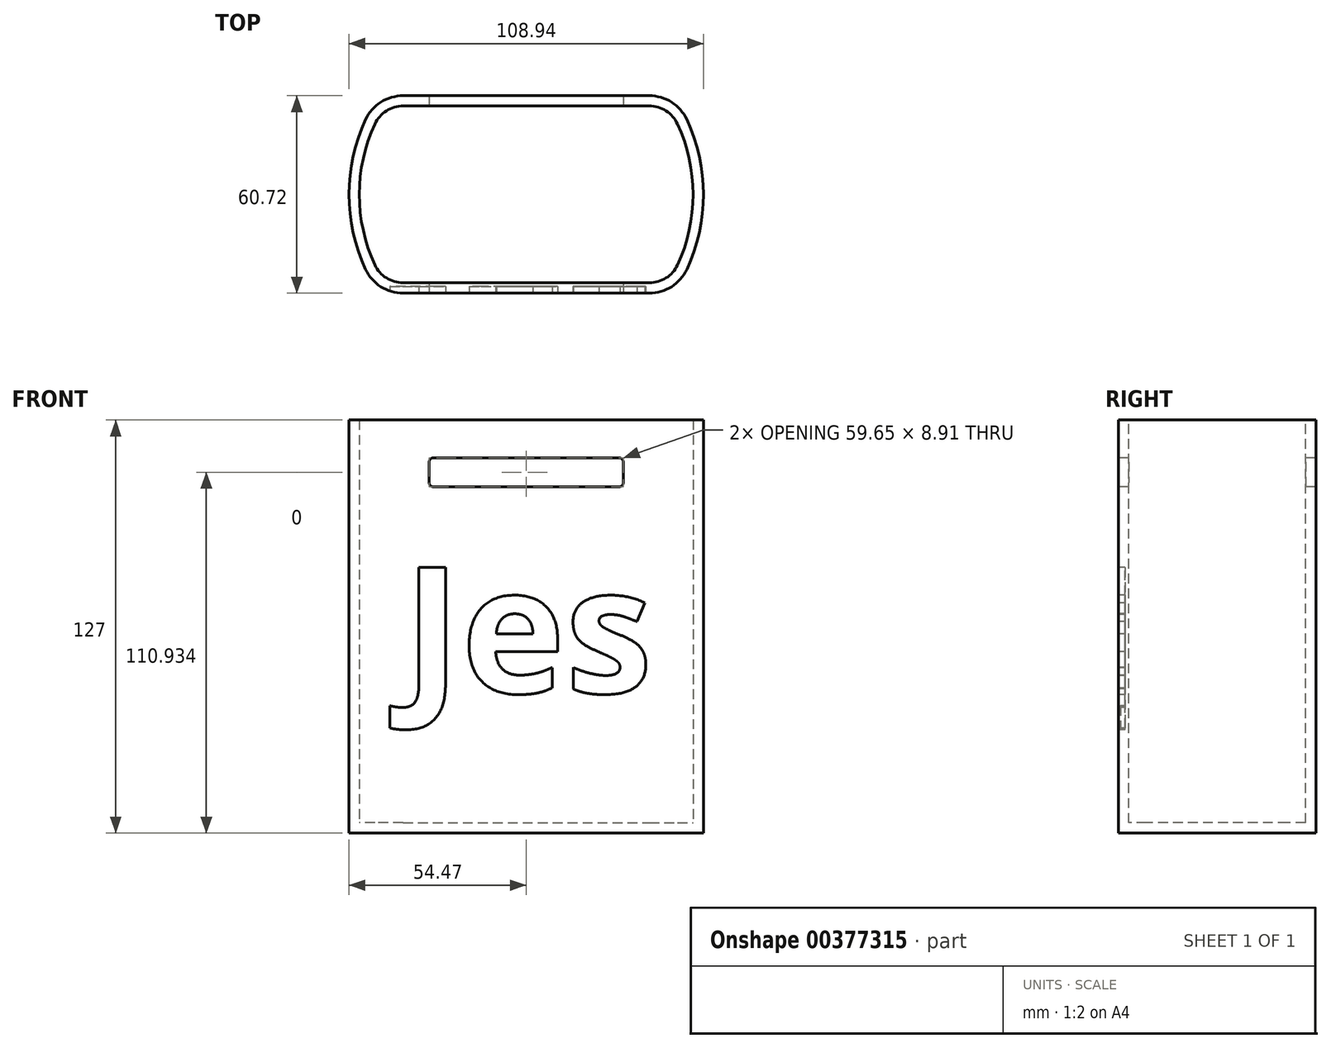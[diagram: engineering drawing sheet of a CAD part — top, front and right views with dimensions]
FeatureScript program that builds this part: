
annotation { "Feature Type Name" : "Feature", "Feature Type Description" : "" }
export const myFeature = defineFeature(function(context is Context, id is Id, definition is map)
    precondition{}
    {
        {
            var Q0;
            Q0=qCreatedBy(makeId("Top.planeOp"),FACE);
            var sketch = newSketch(context, id + "F0", { "sketchPlane" : qUnion([Q0])});
            skArc(sketch, "E0", {"start": v(-49.36, 23.02) * mm, "mid": v(-54.47, 0) * mm, "end": v(-49.36, -23.02) * mm});
            skLineSegment(sketch, "E1", {"start": v(-37.85, 30.36) * mm, "end": v(37.85, 30.36) * mm});
            skLineSegment(sketch, "E2", {"start": v(-54.47, 0) * mm, "end": v(54.47, 0) * mm, "construction": true});
            skLineSegment(sketch, "E3.MirrorCS", {"start": v(-37.85, -30.36) * mm, "end": v(37.85, -30.36) * mm});
            skArc(sketch, "E4.trimOffspring", {"start": v(49.36, -23.02) * mm, "mid": v(54.47, 0) * mm, "end": v(49.36, 23.02) * mm});
            skPoint(sketch, "E5.visualSharp", {"position": v(-45.22, 30.36) * mm});
            skArc(sketch, "E5.filletArc", {"start": v(-37.85, 30.36) * mm, "mid": v(-44.67, 28.37) * mm, "end": v(-49.36, 23.02) * mm});
            skPoint(sketch, "E6.visualSharp", {"position": v(45.22, 30.36) * mm});
            skArc(sketch, "E6.filletArc", {"start": v(49.36, 23.02) * mm, "mid": v(44.67, 28.37) * mm, "end": v(37.85, 30.36) * mm});
            skPoint(sketch, "E7.visualSharp", {"position": v(-45.22, -30.36) * mm});
            skArc(sketch, "E7.filletArc", {"start": v(-49.36, -23.02) * mm, "mid": v(-44.67, -28.37) * mm, "end": v(-37.85, -30.36) * mm});
            skPoint(sketch, "E8.visualSharp", {"position": v(45.22, -30.36) * mm});
            skArc(sketch, "E8.filletArc", {"start": v(37.85, -30.36) * mm, "mid": v(44.67, -28.37) * mm, "end": v(49.36, -23.02) * mm});
            skSolve(sketch);
        }
        {
            var Q0;
            Q0=makeQuery(id+"F0.imprint","IMPRINT",FACE,{"disambiguationData":[TD([[makeQuery(id+"F0.imprint","IMPRINT",EDGE,{"derivedFrom":sQuery(id+"F0.wireOp",EDGE,"E0")}),1.0]])]});
            extrude(context, id + "F1", {"entities" : qUnion([Q0]), "depth" : 127 * mm});
        }
        {
            var Q0;
            Q0=makeQuery(id+"F1.opExtrude","CAP_FACE",FACE,{"disambiguationData":[OSD([sQuery(id+"F0.wireOp",EDGE,"E0"),sQuery(id+"F0.wireOp",EDGE,"E1"),sQuery(id+"F0.wireOp",EDGE,"E3.MirrorCS"),sQuery(id+"F0.wireOp",EDGE,"E4.trimOffspring"),sQuery(id+"F0.wireOp",EDGE,"E5.filletArc"),sQuery(id+"F0.wireOp",EDGE,"E6.filletArc"),sQuery(id+"F0.wireOp",EDGE,"E7.filletArc"),sQuery(id+"F0.wireOp",EDGE,"E8.filletArc")])],"isStart":false});
            shell(context, id + "F2", {"entities" : qUnion([Q0]), "thickness" : 3.17 * mm});
        }
        {
            var Q0;
            Q0=makeQuery(id+"F1.opExtrude","SWEPT_FACE",FACE,{"disambiguationData":[OSD([sQuery(id+"F0.wireOp",EDGE,"E3.MirrorCS")])]});
            var sketch = newSketch(context, id + "F3", { "sketchPlane" : qUnion([Q0])});
            skText(sketch, "E9", { "text": "Jes", "fontName": "OpenSans-Bold.ttf"});
            const initialGuessF3  = {"E9": [-0.03785, 0.04312, 1, 0, 0.0389]};
            skSetInitialGuess(sketch, initialGuessF3);
            skSolve(sketch);
        }
        {
            var Q0;
            Q0 = qSketchRegion(id + "F3", true);
            extrude(context, id + "F4", {"entities" : qUnion([Q0]), "operationType" : NewBodyOperationType.REMOVE, "oppositeDirection" : true, "depth" : 2.03 * mm});
        }
        {
            var Q0;
            {var subQ1=sQuery(id+"F0.wireOp",EDGE,"E7.filletArc");var subQ5=sQuery(id+"F0.wireOp",EDGE,"E3.MirrorCS");Q0=makeQuery(id+"F4.boolean.opBoolean","SPLIT",FACE,{"disambiguationData":[TD([makeQuery(id+"F1.opExtrude","SWEPT_FACE",FACE,{"disambiguationData":[OSD([subQ1])]})])],"derivedFrom":makeQuery(id+"F1.opExtrude","SWEPT_FACE",FACE,{"disambiguationData":[OSD([subQ5])]})});}
            var sketch = newSketch(context, id + "F5", { "sketchPlane" : qUnion([Q0])});
            skLineSegment(sketch, "E10.bottom", {"start": v(28.55, 106.48) * mm, "end": v(-28.55, 106.48) * mm});
            skLineSegment(sketch, "E10.top", {"start": v(28.55, 115.39) * mm, "end": v(-28.55, 115.39) * mm});
            skLineSegment(sketch, "E10.left", {"start": v(29.82, 107.75) * mm, "end": v(29.82, 114.12) * mm});
            skLineSegment(sketch, "E10.right", {"start": v(-29.82, 107.75) * mm, "end": v(-29.82, 114.12) * mm});
            skPoint(sketch, "E10.middle", {"position": v(0, 110.93) * mm});
            skPoint(sketch, "E10.middle.positionSnap0", {"position": v(0, 127) * mm});
            skPoint(sketch, "E10.centerSnap0", {"position": v(0, 127) * mm});
            skPoint(sketch, "E11.visualSharp", {"position": v(-29.82, 115.39) * mm});
            skArc(sketch, "E11.filletArc", {"start": v(-28.55, 115.39) * mm, "mid": v(-29.45, 115.02) * mm, "end": v(-29.82, 114.12) * mm});
            skPoint(sketch, "E12.visualSharp", {"position": v(-29.82, 106.48) * mm});
            skArc(sketch, "E12.filletArc", {"start": v(-29.82, 107.75) * mm, "mid": v(-29.45, 106.85) * mm, "end": v(-28.55, 106.48) * mm});
            skPoint(sketch, "E13.visualSharp", {"position": v(29.82, 115.39) * mm});
            skArc(sketch, "E13.filletArc", {"start": v(29.82, 114.12) * mm, "mid": v(29.45, 115.02) * mm, "end": v(28.55, 115.39) * mm});
            skPoint(sketch, "E14.visualSharp", {"position": v(29.82, 106.48) * mm});
            skArc(sketch, "E14.filletArc", {"start": v(28.55, 106.48) * mm, "mid": v(29.45, 106.85) * mm, "end": v(29.82, 107.75) * mm});
            skSolve(sketch);
        }
        {
            var Q0;
            Q0=makeQuery(id+"F5.imprint","IMPRINT",FACE,{"disambiguationData":[TD([[makeQuery(id+"F5.imprint","IMPRINT",EDGE,{"derivedFrom":sQuery(id+"F5.wireOp",EDGE,"E10.bottom")}),-1.0]])]});
            extrude(context, id + "F6", {"entities" : qUnion([Q0]), "operationType" : NewBodyOperationType.REMOVE, "endBound" : BoundingType.THROUGH_ALL, "oppositeDirection" : true, "depth" : 25.4 * mm});
        }
    });
